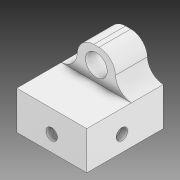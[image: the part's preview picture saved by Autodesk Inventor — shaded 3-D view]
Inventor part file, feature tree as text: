
AUTODESK INVENTOR PART (.ipt)
format: ipt  version: 2020 (Build 240168000, 168)  size: 208,896 bytes
history: native  units: mm
features: extrude x7, sketch x7, fillet x2
ambient origin geometry x8: Origin, YZ Plane, XZ Plane, XY Plane, X Axis, Y Axis, Z Axis, Center Point
bodies: Solid1 (feature_tree)
feature tree (16):
  extrude  "Extrusion1"  Depth=5.0mm
  extrude  "Extrusion2"  Depth=2.0mm
  extrude  "Extrusion3"  Depth=22.5mm
  extrude  "Extrusion4"  Depth=45.0mm
  extrude  "Extrusion5"  Depth=5.0mm TaperAngle=0.0deg
  extrude  "Extrusion6"  Depth=30.0mm
  extrude  "Extrusion7"  Depth=25.0mm TaperAngle=0.0deg
  fillet  "Fillet3"  Radius=17.0mm
  fillet  "Fillet4"  Radius=13.0mm
  sketch  "Sketch1"  dims[d1=5.0mm d2=2.0mm]
  sketch  "Sketch2"  dims[d3=2.0mm d4=2.0mm]
  sketch  "Sketch3"  dims[d5=2.0mm d6=22.5mm]
  sketch  "Sketch4"  dims[d7=22.5mm d8=45.0mm]
  sketch  "Sketch5"  dims[d9=25.0mm d10=0.0mm d11=5.0mm d12=0.0mm]
  sketch  "Sketch6"  dims[d14=20.0mm d15=30.0mm]
  sketch  "Sketch7"  dims[d16=15.0mm d17=25.0mm d18=0.0mm d19=17.0mm d20=13.0mm d21=40.0mm d22=0.0mm d25=9.0mm d26=12.5mm d27=0.0mm d28=0.0mm d29=9.0mm d30=12.5mm d31=0.0mm d32=0.0mm d33=5.0mm d34=5.0mm d35=0.0mm d36=13.0mm d37=13.0mm]
